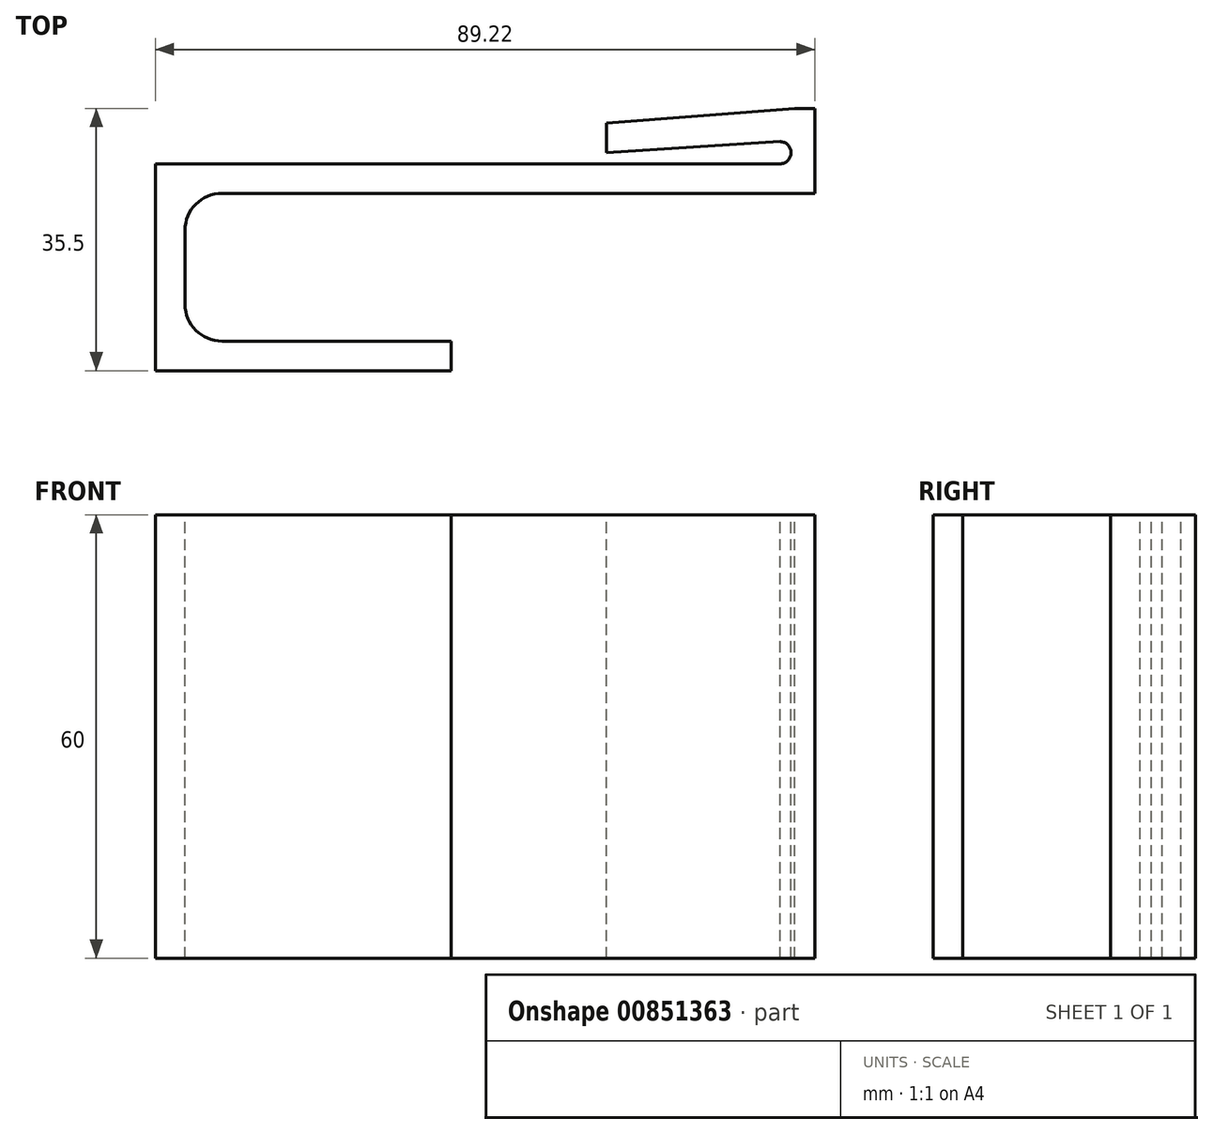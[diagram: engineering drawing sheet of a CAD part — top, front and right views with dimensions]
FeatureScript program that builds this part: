
annotation { "Feature Type Name" : "Feature", "Feature Type Description" : "" }
export const myFeature = defineFeature(function(context is Context, id is Id, definition is map)
    precondition{}
    {
        {
            var Q0;
            Q0=qCreatedBy(makeId("Right.planeOp"),FACE);
            var sketch = newSketch(context, id + "F0", { "sketchPlane" : qUnion([Q0])});
            skLineSegment(sketch, "E0", {"start": v(0, 9) * mm, "end": v(0, 89.22) * mm});
            skLineSegment(sketch, "E1", {"start": v(3.5, 86) * mm, "end": v(3.5, 86) * mm});
            skLineSegment(sketch, "E2", {"start": v(-20, 9) * mm, "end": v(-20, 40) * mm});
            skLineSegment(sketch, "E3", {"start": v(-20, 40) * mm, "end": v(-24, 40) * mm});
            skLineSegment(sketch, "E4", {"start": v(-24, 40) * mm, "end": v(-24, 0) * mm});
            skLineSegment(sketch, "E5", {"start": v(-24, 0) * mm, "end": v(0, 0) * mm});
            skLineSegment(sketch, "E6", {"start": v(0, 0) * mm, "end": v(4, 0) * mm});
            skLineSegment(sketch, "E7", {"start": v(4, 0) * mm, "end": v(4, 84.5) * mm});
            skLineSegment(sketch, "E8", {"start": v(-5, 4) * mm, "end": v(-15, 4) * mm});
            skPoint(sketch, "E9.visualSharp", {"position": v(-20, 4) * mm});
            skArc(sketch, "E9.filletArc", {"start": v(-20, 9) * mm, "mid": v(-18.54, 5.46) * mm, "end": v(-15, 4) * mm});
            skPoint(sketch, "E10.visualSharp", {"position": v(0, 4) * mm});
            skArc(sketch, "E10.filletArc", {"start": v(-5, 4) * mm, "mid": v(-1.46, 5.46) * mm, "end": v(0, 9) * mm});
            skPoint(sketch, "E11.visualSharp", {"position": v(4, 86) * mm});
            skPoint(sketch, "E12.visualSharp", {"position": v(9.5, 86) * mm});
            skPoint(sketch, "E13.visualSharp", {"position": v(0, 88) * mm});
            skPoint(sketch, "E14.visualSharp", {"position": v(9, 88) * mm});
            skLineSegment(sketch, "E15", {"start": v(9.5, 61) * mm, "end": v(5.5, 61) * mm});
            skLineSegment(sketch, "E16", {"start": v(5.5, 61) * mm, "end": v(7, 84.5) * mm});
            skLineSegment(sketch, "E17", {"start": v(9.5, 61) * mm, "end": v(11.5, 86.5) * mm});
            skLineSegment(sketch, "E18", {"start": v(0, 89.22) * mm, "end": v(11.5, 89.22) * mm});
            skLineSegment(sketch, "E19", {"start": v(11.5, 89.22) * mm, "end": v(11.5, 86.5) * mm});
            skLineSegment(sketch, "E20", {"start": v(7, 84.5) * mm, "end": v(7, 84.5) * mm});
            skLineSegment(sketch, "E21", {"start": v(5.5, 86) * mm, "end": v(5.5, 86) * mm});
            skArc(sketch, "E22.filletArc", {"start": v(5.5, 86) * mm, "mid": v(4.44, 85.56) * mm, "end": v(4, 84.5) * mm});
            skPoint(sketch, "E23.visualSharp", {"position": v(7, 86) * mm});
            skArc(sketch, "E23.filletArc", {"start": v(7, 84.5) * mm, "mid": v(6.56, 85.56) * mm, "end": v(5.5, 86) * mm});
            skSolve(sketch);
        }
        {
            var Q0;
            Q0 = qSketchRegion(id + "F0", true);
            extrude(context, id + "F1", {"entities" : qUnion([Q0]), "depth" : 30 * mm, "offsetDistance" : 25 * mm, "hasSecondDirection" : true, "secondDirectionOppositeDirection" : true, "secondDirectionDepth" : 30 * mm});
        }
        {
            var Q0;
            Q0=makeQuery(id+"F1.opExtrude","SWEPT_BODY",BODY,{"disambiguationData":[OSD([sQuery(id+"F0.wireOp",EDGE,"E0"),sQuery(id+"F0.wireOp",EDGE,"E2"),sQuery(id+"F0.wireOp",EDGE,"E3"),sQuery(id+"F0.wireOp",EDGE,"E4"),sQuery(id+"F0.wireOp",EDGE,"E5"),sQuery(id+"F0.wireOp",EDGE,"E6"),sQuery(id+"F0.wireOp",EDGE,"E7"),sQuery(id+"F0.wireOp",EDGE,"E8"),sQuery(id+"F0.wireOp",EDGE,"E9.filletArc"),sQuery(id+"F0.wireOp",EDGE,"E10.filletArc"),sQuery(id+"F0.wireOp",EDGE,"E15"),sQuery(id+"F0.wireOp",EDGE,"E16"),sQuery(id+"F0.wireOp",EDGE,"E17"),sQuery(id+"F0.wireOp",EDGE,"E18"),sQuery(id+"F0.wireOp",EDGE,"E19"),sQuery(id+"F0.wireOp",EDGE,"E22.filletArc"),sQuery(id+"F0.wireOp",EDGE,"E23.filletArc")])]});
            var Q1;
            Q1=makeQuery(id+"F1.opExtrude","CAP_EDGE",EDGE,{"disambiguationData":[OSD([sQuery(id+"F0.wireOp",EDGE,"E5"),sQuery(id+"F0.wireOp",EDGE,"E6")])],"isStart":false});
            transform(context, id + "F2", {"entities" : qUnion([Q0]), "transformType" : TransformType.ROTATION, "transformAxis" : qUnion([Q1]), "angle" : 90 * degree, "makeCopy" : false});
        }
    });
